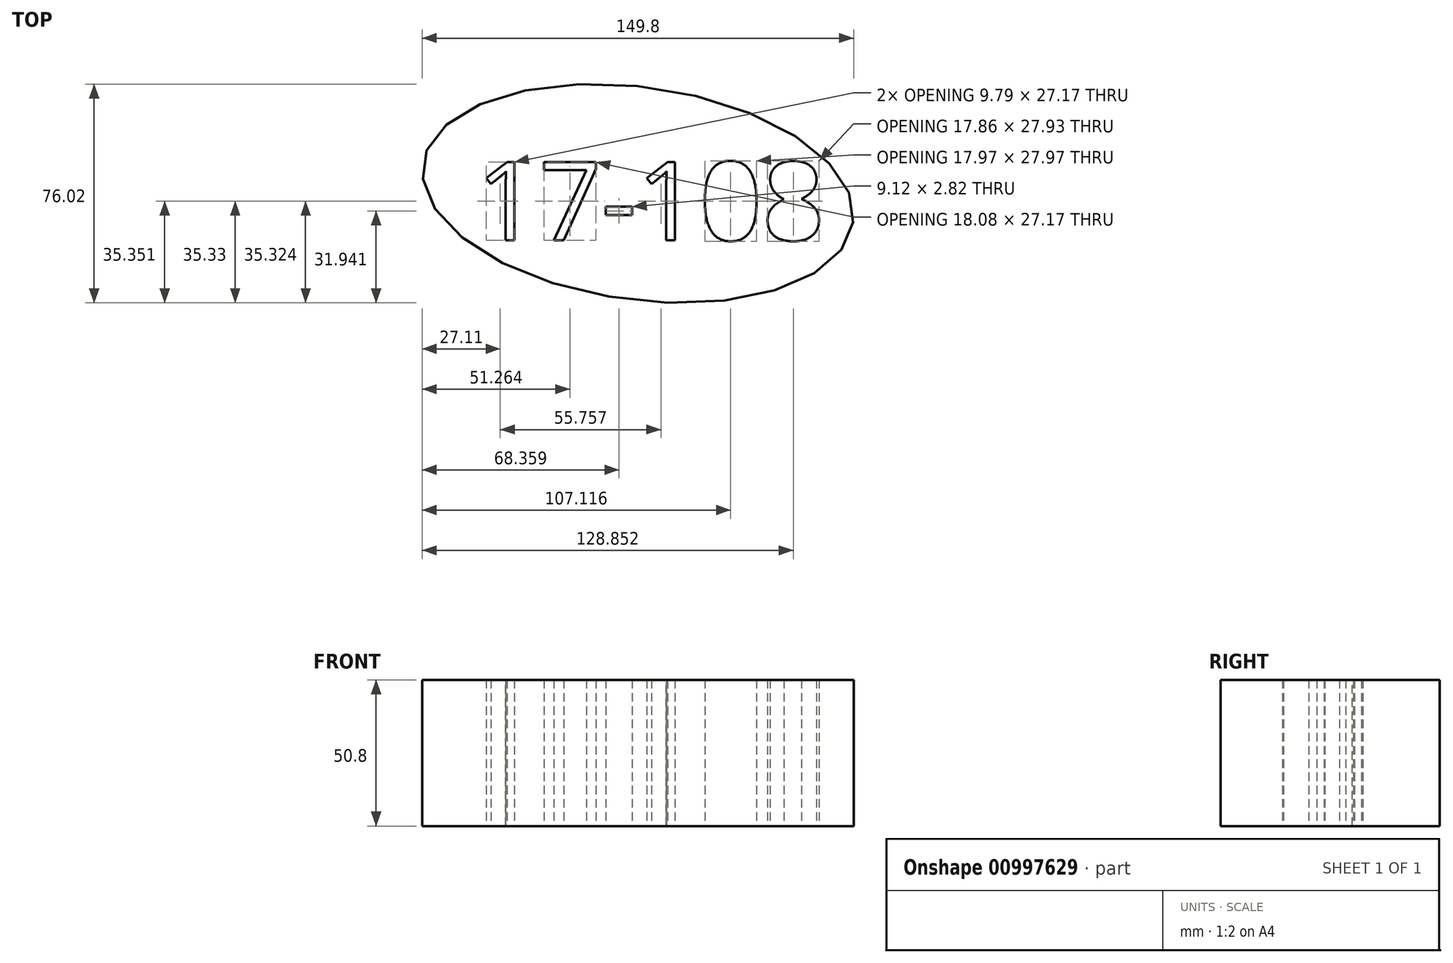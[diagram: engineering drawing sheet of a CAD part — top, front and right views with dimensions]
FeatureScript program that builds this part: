
annotation { "Feature Type Name" : "Feature", "Feature Type Description" : "" }
export const myFeature = defineFeature(function(context is Context, id is Id, definition is map)
    precondition{}
    {
        {
            var Q0;
            Q0=qCreatedBy(makeId("Top.planeOp"),FACE);
            var sketch = newSketch(context, id + "F0", { "sketchPlane" : qUnion([Q0])});
            skEllipse(sketch, "E0", {"center": v(0, 0) * mm, "majorRadius": 75.4 * mm, "minorRadius": 36.98 * mm, "majorAxis": v(1, -0.13)});
            skText(sketch, "E1", { "text": "17-108", "fontName": "OpenSans-Regular.ttf"});
            const initialGuessF0  = {"E1": [-0.05618, -0.01627, 1, 0, 0.0274]};
            skSetInitialGuess(sketch, initialGuessF0);
            skSolve(sketch);
        }
        {
            var Q0;
            Q0=makeQuery(id+"F0.imprint","IMPRINT",FACE,{"disambiguationData":[TD([[makeQuery(id+"F0.imprint","IMPRINT",EDGE,{"derivedFrom":sQuery(id+"F0.wireOp",EDGE,"E0")}),1.0]])]});
            extrude(context, id + "F1", {"entities" : qUnion([Q0]), "depth" : 25.4 * mm, "offsetDistance" : 25.4 * mm});
        }
        {
            var Q0;
            Q0 = qSketchRegion(id + "F0", true);
            extrude(context, id + "F2", {"entities" : qUnion([Q0]), "operationType" : NewBodyOperationType.ADD, "oppositeDirection" : true, "depth" : 25.4 * mm, "offsetDistance" : 25.4 * mm});
        }
    });
